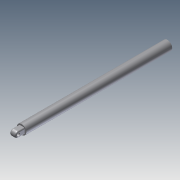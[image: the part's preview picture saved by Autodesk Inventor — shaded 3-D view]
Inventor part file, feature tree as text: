
AUTODESK INVENTOR PART (.ipt)
format: ipt  version: 2011 (Build 150239000, 239)  size: 176,128 bytes
history: native  units: in
note: dims shown in document units (in); Inventor stores cm internally (conversion verified against a paired STEP export)
features: extrude x13, sketch x13, fillet x2
ambient origin geometry x8: Origin, YZ Plane, XZ Plane, XY Plane, X Axis, Y Axis, Z Axis, Center Point
bodies: Solid1 (feature_tree)
feature tree (28):
  extrude  "Extrusion1"  Depth=0.5in TaperAngle=0.0deg
  extrude  "Extrusion2"  Depth=0.5in TaperAngle=0.0deg
  extrude  "Extrusion3"  Depth=0.5in TaperAngle=0.0deg
  extrude  "Extrusion4"  Depth=0.125in
  extrude  "Extrusion5"  Depth=0.25in
  extrude  "Extrusion6"  Depth=0.125in
  fillet  "Fillet1"  Radius=0.78in
  extrude  "Extrusion7"  Depth=4.0in TaperAngle=0.0deg
  extrude  "Extrusion8"  Depth=0.5in TaperAngle=0.0deg
  extrude  "Extrusion9"  Depth=0.5in TaperAngle=0.0deg
  extrude  "Extrusion10"  Depth=0.125in
  extrude  "Extrusion11"  Depth=8.0in TaperAngle=0.0deg
  fillet  "Fillet2"  [1 undecoded]
  extrude  "Extrusion12"  [1 undecoded]
  extrude  "Extrusion13"  [1 undecoded]
  sketch  "Sketch1"  dims[d0=4.0in d1=0.0in d2=0.5in d3=0.0in]
  sketch  "Sketch2"  dims[d4=0.25in d5=0.5in d6=0.0in]
  sketch  "Sketch3"  dims[d7=0.5in d8=0.0in d9=0.5in d10=0.0in]
  sketch  "Sketch4"  dims[d11=0.125in d12=0.125in]
  sketch  "Sketch5"  dims[d13=0.25in d14=0.25in]
  sketch  "Sketch6"  dims[d15=0.5in d16=0.0in d17=0.125in d18=0.78in]
  sketch  "Sketch7"  dims[d19=4.0in d20=0.0in d21=4.0in d22=0.0in]
  sketch  "Sketch8"  dims[d23=0.5in d24=0.5in d25=0.0in]
  sketch  "Sketch9"  dims[d26=0.25in d27=0.5in d28=0.0in]
  sketch  "Sketch10"  dims[d29=0.5in d30=0.0in d31=0.125in]
  sketch  "Sketch11"  dims[d32=0.5in d33=0.0in d34=8.0in d35=0.0in]
  sketch  "Sketch12"
  sketch  "Sketch13"
note: 3 required parameter values undecoded (feature->parameter linkage not recoverable at this tier; creation-order binding heuristic only, values carry confidence <= 0.55)
